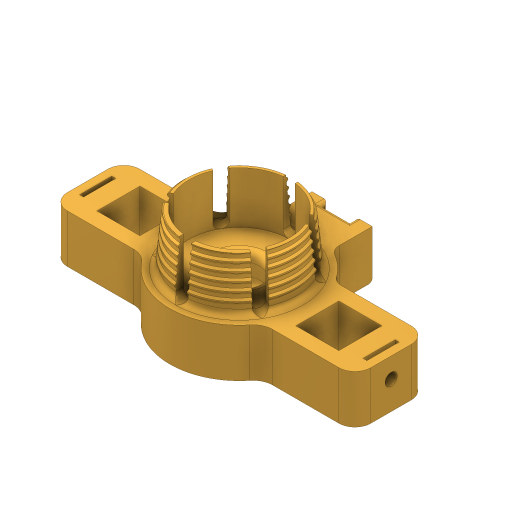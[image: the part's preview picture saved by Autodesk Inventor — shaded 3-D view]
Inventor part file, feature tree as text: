
AUTODESK INVENTOR PART (.ipt)
format: ipt  version: 2023 (Build 270158000, 158)  size: 1,312,768 bytes
history: native  units: mm
features: sketch x7, fillet x6, extrude x5, hole x3, helix x2, direct_edit x2, draft x1, mirror x1, chamfer x1, other x1, revolve x1
ambient origin geometry x8: Origin, YZ Plane, XZ Plane, XY Plane, X Axis, Y Axis, Z Axis, Center Point
bodies: Solid1 (feature_tree)
feature tree (30):
  extrude  "Extrusion1"  Depth=26.5mm
  draft  "FaceDraft1"
  sketch  "Sketch2"  dims[d34=0.0mm d35=0.0mm d56=8.726646mm]
  helix  "Coil3"  [1 undecoded]
  helix  "Coil4"  [1 undecoded]
  direct_edit  "Direct Edit2"
  extrude  "Extrusion2"  Depth=8.726646mm
  extrude  "Extrusion13"  TaperAngle=90.0deg  [1 undecoded]
  extrude  "Extrusion14"  Depth=34.58632mm
  hole  "Hole3"  [1 undecoded]
  hole  "Hole4"  [1 undecoded]
  fillet  "Fillet11"  Radius=60.0mm
  hole  "Hole6"  [1 undecoded]
  mirror  "Mirror3"
  extrude  "Extrusion15"  Depth=3.0mm
  direct_edit  "Direct Edit3"
  fillet  "Fillet13"  Radius=20.0mm
  fillet  "Fillet15"  Radius=18.0mm
  fillet  "Fillet16"  Radius=10.7mm
  fillet  "Fillet17"  Radius=10.0mm
  fillet  "Fillet18"  Radius=15.0mm
  chamfer  "Chamfer3"  Distance=10.0mm
  sketch  "Sketch1"  dims[d0=25.0mm d1=26.5mm d2=12.875mm d3=0.0mm d4=1.047198mm]
  sketch  "Sketch3"  dims[d62=2.0mm d63=10.15mm d64=10.0mm d65=1.047198mm]
  sketch  "Sketch13"  dims[d66=90.0deg d67=90.0deg d68=0.0mm d69=0.0mm d70=2.0mm d71=3.0mm d72=10.0mm d73=-1.047198mm d74=90.0deg d75=90.0deg d76=0.0mm d77=0.0mm]
  sketch  "Sketch14"  dims[d79=-0.127mm d145=34.58632mm]
  sketch  "Sketch16"  dims[d150=120.0deg d151=120.0deg]
  sketch  "Sketch17"  dims[d153=21.6866mm d157=12.0mm d158=0.0mm d160=60.0mm d162=360.0deg d164=0.0mm d165=0.0mm d179=5.3mm d180=6.0mm d181=4.0mm d182=2.0mm d183=90.0deg d184=5.0mm d185=0.0mm d186=10.0mm d187=6.0mm d188=4.0mm d189=2.0mm d190=90.0deg d191=7.0mm d192=0.0mm d193=2.0mm d194=20.0mm d195=18.0mm d196=10.7mm d197=10.0mm d206=15.0mm d207=10.0mm d208=7.0mm d209=10.0mm d210=1.0mm d211=0.0mm d212=-4.363323mm d213=1.0mm d215=1.5mm d216=3.0mm d217=8.0mm d219=1.0mm d220=5.0mm d221=3.0mm d222=6.0mm d223=4.0mm d224=2.0mm d225=90.0deg d226=6.5mm d227=0.0mm d228=3.0mm d229=5.0mm d230=4.0mm d231=3.0mm d232=2.0mm d233=45.0deg d109=0.5mm d110=0.872665mm d111=0.5mm d112=0.872665mm]
  other  "Size2"
  revolve  "Rotate1"  [1 undecoded]
note: 7 required parameter values undecoded (feature->parameter linkage not recoverable at this tier; creation-order binding heuristic only, values carry confidence <= 0.55)